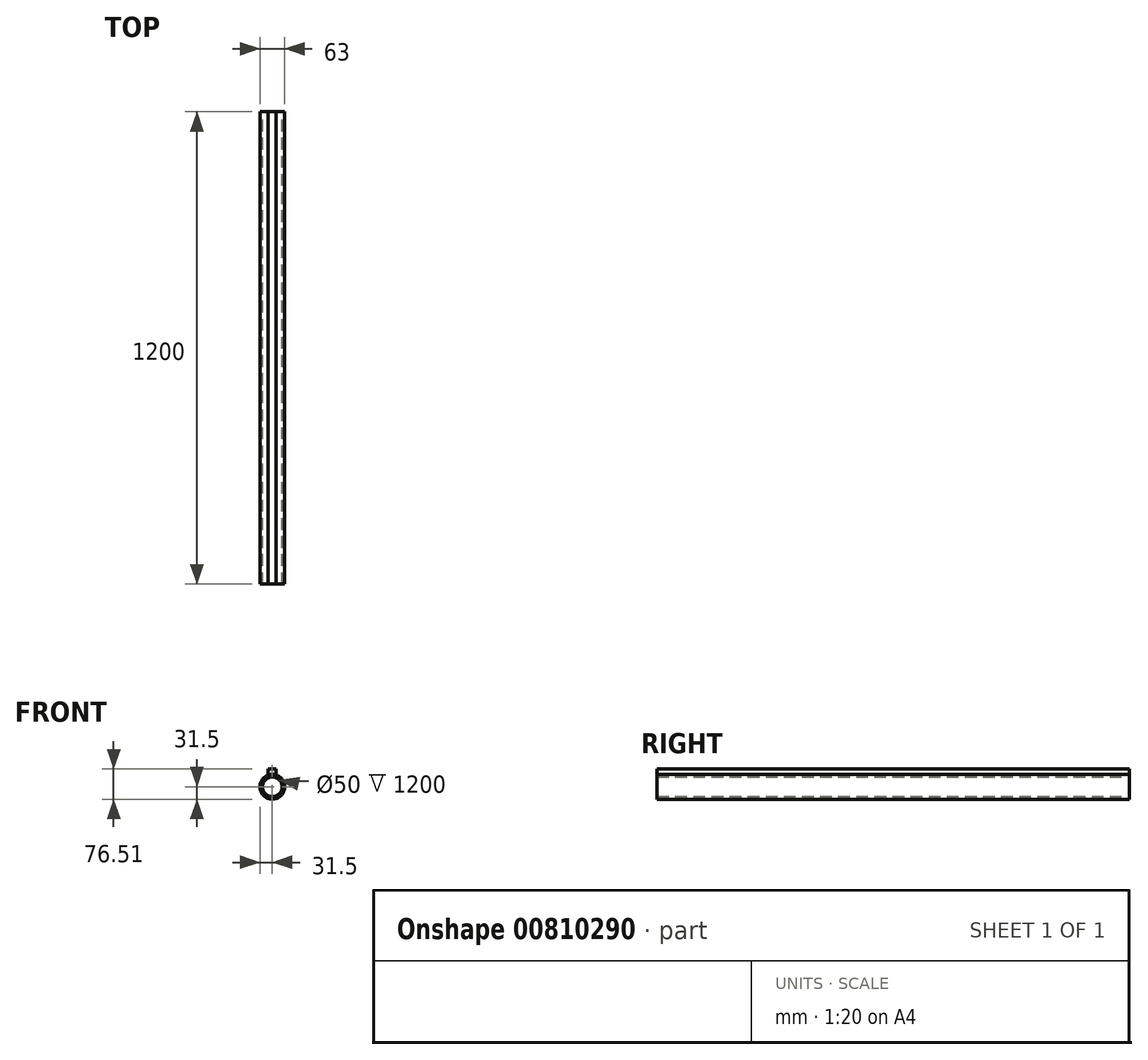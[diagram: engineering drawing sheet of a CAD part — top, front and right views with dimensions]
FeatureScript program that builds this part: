
annotation { "Feature Type Name" : "Feature", "Feature Type Description" : "" }
export const myFeature = defineFeature(function(context is Context, id is Id, definition is map)
    precondition{}
    {
        {
            var Q0;
            Q0=qCreatedBy(makeId("Front.planeOp"),FACE);
            var sketch = newSketch(context, id + "F0", { "sketchPlane" : qUnion([Q0])});
            skCircle(sketch, "E0", {"center": v(0, 0) * mm, "radius": 31.5 * mm});
            skCircle(sketch, "E1", {"center": v(0, 0) * mm, "radius": 25 * mm});
            skLineSegment(sketch, "E2", {"start": v(0, 0) * mm, "end": v(0, 25) * mm});
            skLineSegment(sketch, "E3", {"start": v(0, 0) * mm, "end": v(-25, 0) * mm});
            skLineSegment(sketch, "E4", {"start": v(0, 0) * mm, "end": v(25, 0) * mm});
            skLineSegment(sketch, "E5", {"start": v(0, 0) * mm, "end": v(0, -25) * mm});
            skSolve(sketch);
        }
        {
            var Q0;
            Q0=makeQuery(id+"F0.imprint","IMPRINT",FACE,{"disambiguationData":[TD([[makeQuery(id+"F0.imprint","IMPRINT",EDGE,{"derivedFrom":sQuery(id+"F0.wireOp",EDGE,"E0")}),1.0]])]});
            extrude(context, id + "F1", {"entities" : qUnion([Q0]), "endBound" : BoundingType.SYMMETRIC, "depth" : 1200 * mm, "offsetDistance" : 25 * mm});
        }
        {
            var Q0;
            Q0=qCreatedBy(makeId("Front.planeOp"),FACE);
            var sketch = newSketch(context, id + "F2", { "sketchPlane" : qUnion([Q0])});
            skLineSegment(sketch, "E6.bottom", {"start": v(-10.31, 45.01) * mm, "end": v(9.66, 45.01) * mm});
            skLineSegment(sketch, "E6.top", {"start": v(-10.31, 31.55) * mm, "end": v(9.66, 31.55) * mm});
            skLineSegment(sketch, "E6.left", {"start": v(-10.31, 45.01) * mm, "end": v(-10.31, 31.55) * mm});
            skLineSegment(sketch, "E6.right", {"start": v(9.66, 45.01) * mm, "end": v(9.66, 31.55) * mm});
            skLineSegment(sketch, "E7", {"start": v(0, 31.55) * mm, "end": v(0, 29.5) * mm});
            skCircle(sketch, "E8", {"center": v(0, 0) * mm, "radius": 31.5 * mm});
            skPoint(sketch, "E9", {"position": v(-0.32, 31.55) * mm});
            skSolve(sketch);
        }
        {
            var Q0;
            Q0=makeQuery(id+"F2.imprint","IMPRINT",FACE,{"disambiguationData":[TD([[makeQuery(id+"F2.imprint","IMPRINT",EDGE,{"derivedFrom":sQuery(id+"F2.wireOp",EDGE,"E6.bottom")}),-1.0]])]});
            extrude(context, id + "F3", {"entities" : qUnion([Q0]), "endBound" : BoundingType.SYMMETRIC, "depth" : 1200 * mm, "offsetDistance" : 25 * mm});
        }
    });
